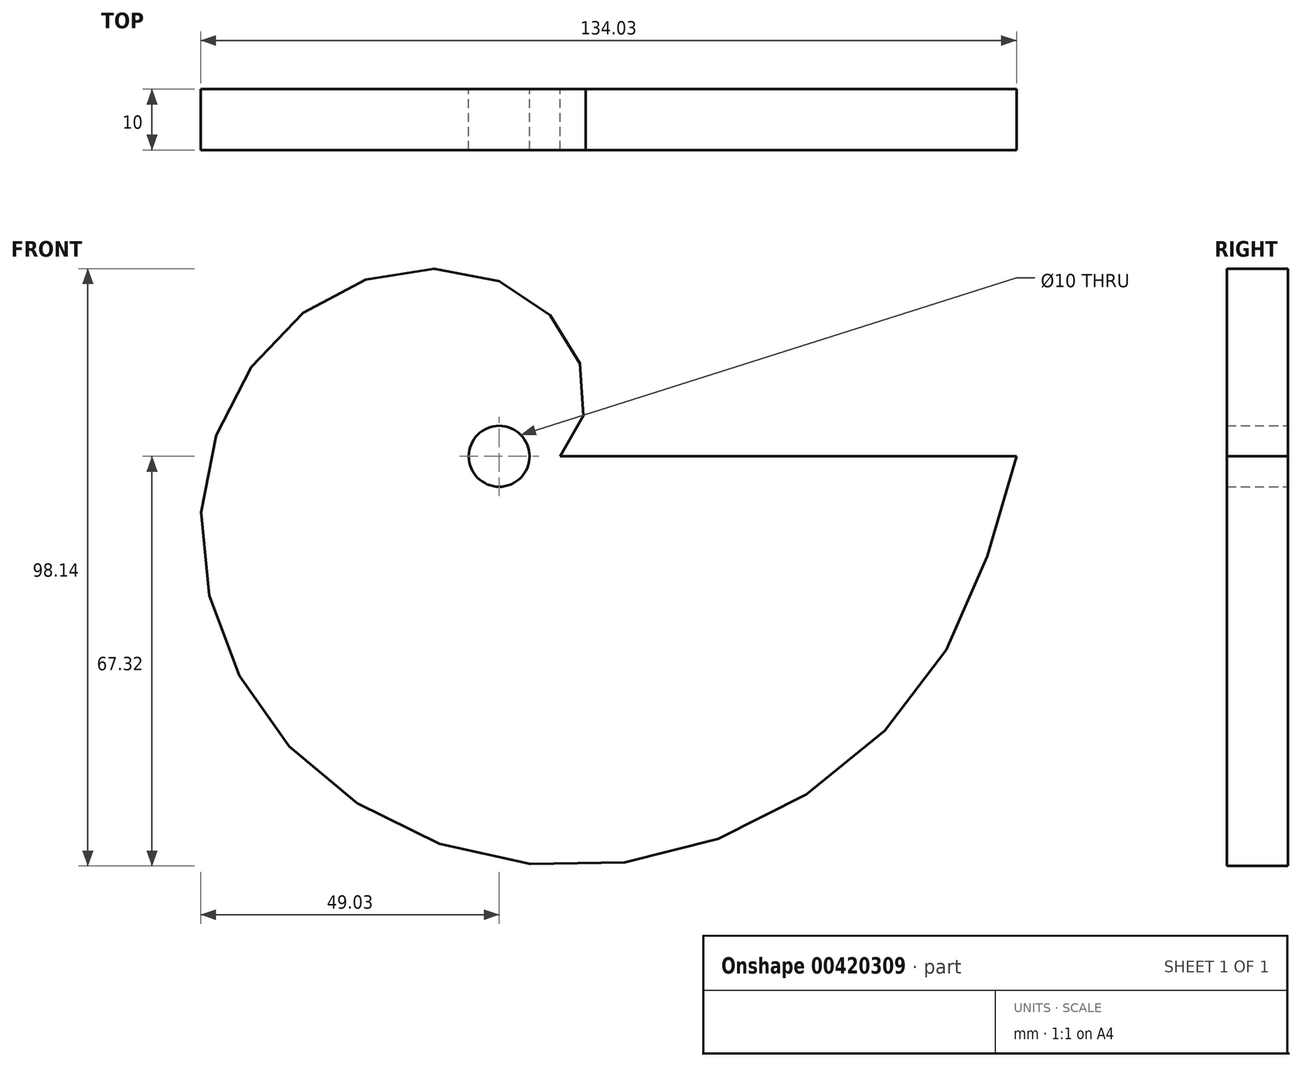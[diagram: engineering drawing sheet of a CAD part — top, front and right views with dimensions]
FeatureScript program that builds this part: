
annotation { "Feature Type Name" : "Feature", "Feature Type Description" : "" }
export const myFeature = defineFeature(function(context is Context, id is Id, definition is map)
    precondition{}
    {
        {
            var Q0;
            Q0=qCreatedBy(makeId("Front.planeOp"),FACE);
            var sketch = newSketch(context, id + "F0", { "sketchPlane" : qUnion([Q0])});
            skFitSpline(sketch, "E0", {"points": [v(85, 0) * mm, v(73.18, -32.31) * mm, v(50.14, -55.77) * mm, v(21.5, -66.62) * mm, v(-6.69, -64.66) * mm, v(-30.13, -51.89) * mm, v(-44.42, -32.44) * mm, v(-49, -9.9) * mm, v(-44.07, 9.1) * mm, v(-32.48, 23.35) * mm, v(-17.88, 30.09) * mm, v(-3.1, 29.84) * mm, v(7.9, 23.72) * mm, v(13.4, 14.84) * mm, v(13.68, 6.15) * mm, v(10, 0) * mm], "startDerivative": vector(-102.9, -382.76) * mm, "endDerivative": vector(-110.4, -141.16) * mm});
            skLineSegment(sketch, "E1", {"start": v(10, 0) * mm, "end": v(85, 0) * mm});
            skCircle(sketch, "E2", {"center": v(0, 0) * mm, "radius": 5 * mm});
            skSolve(sketch);
        }
        {
            var Q0;
            Q0=makeQuery(id+"F0.imprint","IMPRINT",FACE,{"disambiguationData":[TD([[makeQuery(id+"F0.imprint","IMPRINT",EDGE,{"derivedFrom":sQuery(id+"F0.wireOp",EDGE,"E0")}),-1.0]])]});
            extrude(context, id + "F1", {"entities" : qUnion([Q0]), "depth" : 10 * mm, "offsetDistance" : 25 * mm});
        }
    });
